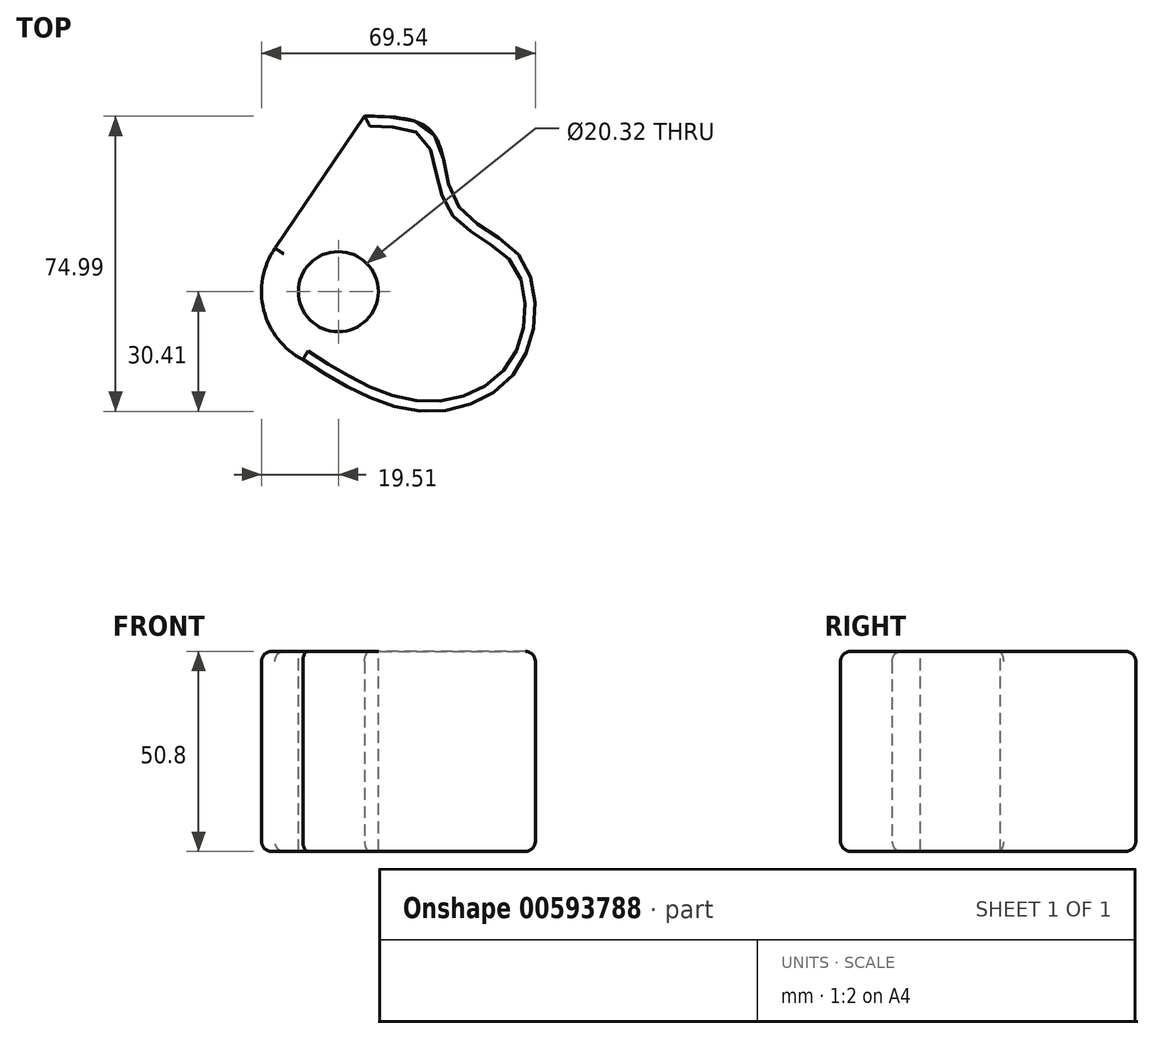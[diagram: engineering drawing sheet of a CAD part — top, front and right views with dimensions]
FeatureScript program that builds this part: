
annotation { "Feature Type Name" : "Feature", "Feature Type Description" : "" }
export const myFeature = defineFeature(function(context is Context, id is Id, definition is map)
    precondition{}
    {
        {
            var Q0;
            Q0=qCreatedBy(makeId("Top.planeOp"),FACE);
            var sketch = newSketch(context, id + "F0", { "sketchPlane" : qUnion([Q0])});
            skArc(sketch, "E0", {"start": v(-16.08, 11.05) * mm, "mid": v(-18.93, -4.72) * mm, "end": v(-9.02, -17.3) * mm});
            skFitSpline(sketch, "E1", {"points": [v(-16.22, 10.84) * mm, v(18.1, 61.46) * mm], "startDerivative": vector(34.31, 50.62) * mm, "endDerivative": vector(34.31, 50.62) * mm});
            skFitSpline(sketch, "E2", {"points": [v(6.66, 44.58) * mm, v(24.08, 40.28) * mm, v(30.23, 22) * mm, v(46.52, 8.42) * mm, v(45.98, -18.92) * mm, v(20.82, -30.32) * mm, v(-12.17, -15.25) * mm], "startDerivative": vector(149.07, -1.72) * mm, "endDerivative": vector(-161, 105.02) * mm});
            skLineSegment(sketch, "E3", {"start": v(-16.08, 11.05) * mm, "end": v(6.66, 44.58) * mm});
            skSolve(sketch);
        }
        {
            var Q0;
            Q0 = qSketchRegion(id + "F0", true);
            extrude(context, id + "F1", {"entities" : qUnion([Q0]), "depth" : 50.8 * mm, "offsetDistance" : 25.4 * mm});
        }
        {
            var Q0;
            Q0=makeQuery(id+"F1.opExtrude","CAP_EDGE",EDGE,{"disambiguationData":[OSD([sQuery(id+"F0.wireOp",EDGE,"E3")])],"isStart":false});
            var Q1;
            Q1=makeQuery(id+"F1.opExtrude","CAP_EDGE",EDGE,{"disambiguationData":[OSD([sQuery(id+"F0.wireOp",EDGE,"E0")])],"isStart":false});
            var Q2;
            Q2=makeQuery(id+"F1.opExtrude","CAP_EDGE",EDGE,{"disambiguationData":[OSD([sQuery(id+"F0.wireOp",EDGE,"E2")])],"isStart":false});
            var Q3;
            Q3=makeQuery(id+"F1.opExtrude","CAP_EDGE",EDGE,{"disambiguationData":[OSD([sQuery(id+"F0.wireOp",EDGE,"E3")])],"isStart":true});
            var Q4;
            Q4=makeQuery(id+"F1.opExtrude","CAP_EDGE",EDGE,{"disambiguationData":[OSD([sQuery(id+"F0.wireOp",EDGE,"E0")])],"isStart":true});
            var Q5;
            Q5=makeQuery(id+"F1.opExtrude","CAP_EDGE",EDGE,{"disambiguationData":[OSD([sQuery(id+"F0.wireOp",EDGE,"E2")])],"isStart":true});
            fillet(context, id + "F2", {"entities" : qUnion([Q0, Q1, Q2, Q3, Q4, Q5]), "radius" : 2.54 * mm, "tangentPropagation" : true, "allowEdgeOverflow" : false});
        }
        {
            var Q0;
            Q0=makeQuery(id+"F1.opExtrude","CAP_FACE",FACE,{"disambiguationData":[OSD([sQuery(id+"F0.wireOp",EDGE,"E0"),sQuery(id+"F0.wireOp",EDGE,"E2"),sQuery(id+"F0.wireOp",EDGE,"E3")])],"isStart":false});
            var sketch = newSketch(context, id + "F3", { "sketchPlane" : qUnion([Q0])});
            skCircle(sketch, "E4", {"center": v(0, 0) * mm, "radius": 7.6 * mm});
            skSolve(sketch);
        }
        {
            var Q0;
            Q0=sQuery(id+"F3.wireOp",VERTEX,"E4.center");
            var Q1;
            Q1=makeQuery(id+"F1.opExtrude","SWEPT_BODY",BODY,{"disambiguationData":[OSD([sQuery(id+"F0.wireOp",EDGE,"E0"),sQuery(id+"F0.wireOp",EDGE,"E2"),sQuery(id+"F0.wireOp",EDGE,"E3")])]});
            hole(context, id + "F4", {"style" : HoleStyle.SIMPLE, "endStyle" : HoleEndStyle.THROUGH, "holeDiameter" : 20.32 * mm, "majorDiameter" : 6.35 * mm, "isTappedThrough" : true, "tappedDepth" : 12.7 * mm, "tapClearance" : 3, "locations" : qUnion([Q0]), "scope" : qUnion([Q1])});
        }
    });
